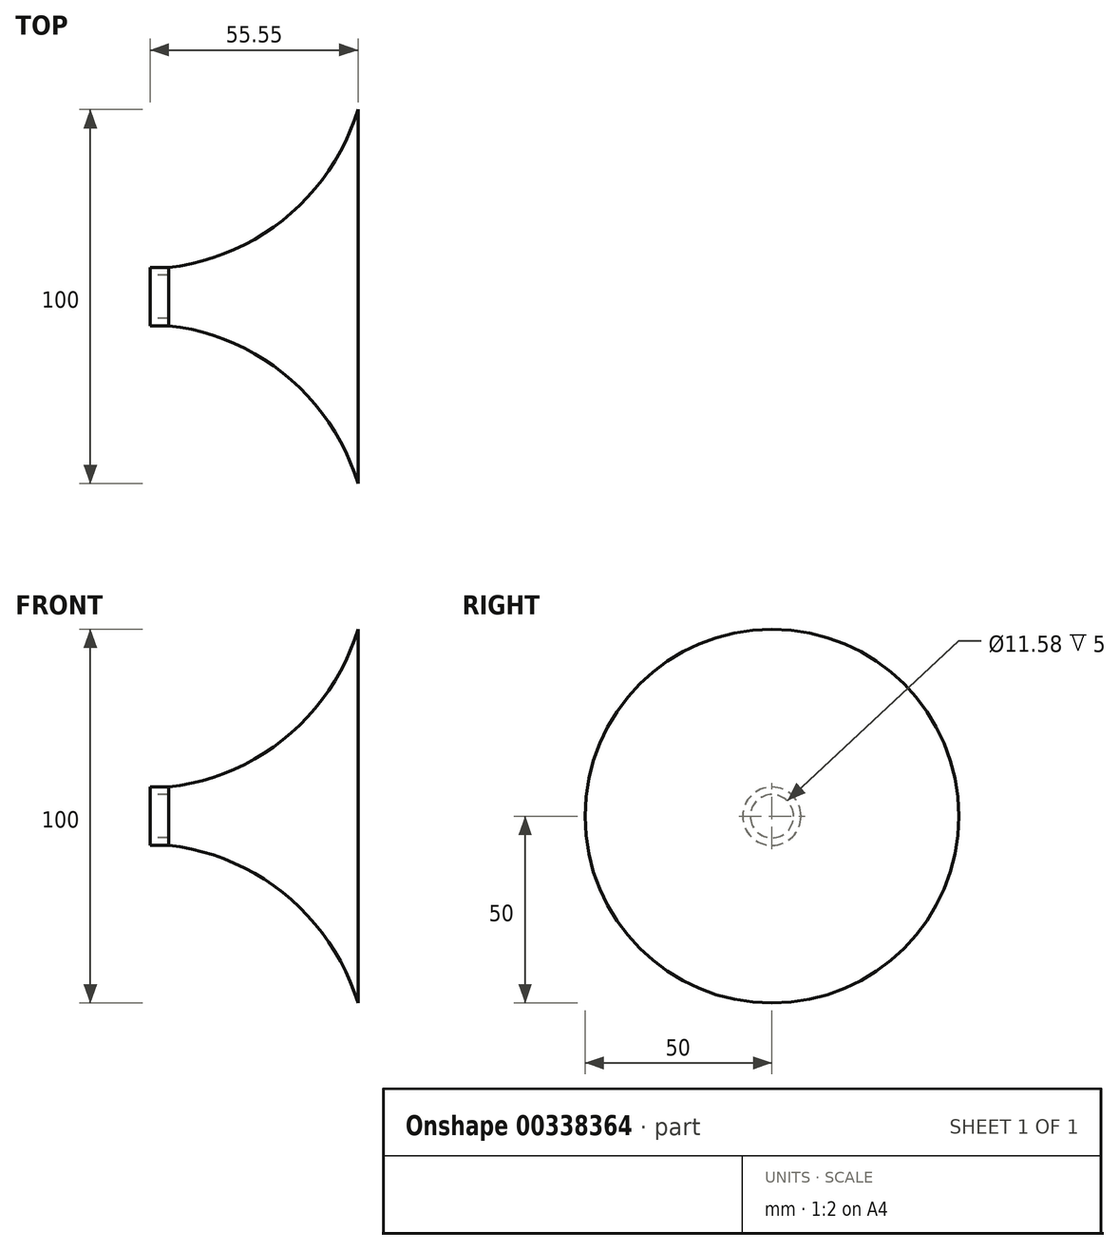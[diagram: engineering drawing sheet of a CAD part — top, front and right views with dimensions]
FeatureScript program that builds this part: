
annotation { "Feature Type Name" : "Feature", "Feature Type Description" : "" }
export const myFeature = defineFeature(function(context is Context, id is Id, definition is map)
    precondition{}
    {
        {
            var Q0;
            Q0=qCreatedBy(makeId("Top.planeOp"),FACE);
            var sketch = newSketch(context, id + "F0", { "sketchPlane" : qUnion([Q0])});
            skLineSegment(sketch, "E0", {"start": v(0, 0) * mm, "end": v(0, 50) * mm});
            skArc(sketch, "E1", {"start": v(-50.55, 7.8) * mm, "mid": v(-18.97, 21.34) * mm, "end": v(0, 50) * mm});
            skLineSegment(sketch, "E2", {"start": v(-50.55, 7.8) * mm, "end": v(-55.55, 7.8) * mm});
            skLineSegment(sketch, "E3", {"start": v(-55.55, 7.8) * mm, "end": v(-55.55, 5.8) * mm});
            skLineSegment(sketch, "E4", {"start": v(-55.55, 5.8) * mm, "end": v(-50.55, 5.8) * mm});
            skLineSegment(sketch, "E5", {"start": v(-50.55, 5.8) * mm, "end": v(-50.55, 0) * mm});
            skLineSegment(sketch, "E6", {"start": v(-50.55, 0) * mm, "end": v(0, 0) * mm});
            skLineSegment(sketch, "E7", {"start": v(-50.55, 0) * mm, "end": v(0, 0) * mm, "construction": true});
            skSolve(sketch);
        }
        {
            var Q0;
            Q0 = qSketchRegion(id + "F0", true);
            var Q1;
            Q1=sQuery(id+"F0.wireOp",EDGE,"E6");
            revolve(context, id + "F1", {"entities" : qUnion([Q0]), "axis" : qUnion([Q1]), "revolveType" : RevolveType.FULL});
        }
    });
